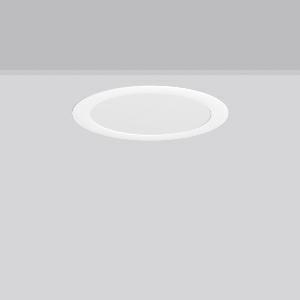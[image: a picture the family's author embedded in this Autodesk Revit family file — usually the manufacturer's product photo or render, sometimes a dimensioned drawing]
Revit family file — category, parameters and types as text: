
# Revit family: toledo_flat_round_e_672226_002_1_04_98b7
name_source: partatom
category: Lighting Fixtures
units: mm (PartAtom-declared; Revit-internal decimal feet)

## family parameters
Cut with Voids When Loaded = No
Host = Face
Light Source = No
Part Type = Normal
Room Calculation Point = No
Round Connector Dimension = Use Diameter
Shared = No

## types (1)
- TOLEDO FLAT round E (1 x LED Modul 840, 2250 lm, 4000)
    Apparent Load = 22 VA
    CIE Flux Codes = 49 80 96 100 100
    Color Rendering = 80
    Color Temperature = 4000
    Default Elevation = 1800 mm
    Description = Series: TOLEDO FLAT round
Ultra thin recessed downlight. For escape route illumination. Housing: die-cast aluminium, powder-coated. Lightguide and diffuser made of non-yellowing plastic (PMMA). Diffuser opal matt plastic. Ceiling installation with spring system. Including separate LED converter with connecting cable 250 mm. Self-contained system with automatic self-test and feedback to the RZB monitoring system MULTIDIGIT. External driver with simple plug-in locking system. 
Colour: white
Diameter: 317 mm
Height: 3 mm
Cut-out diameter: 288 mm
Recess height: 90 mm
Luminaire: recess height: 60-80 mm
Weight: 2.28 kg
Operating mode: maintained power mode
Duration time: 3 h
Lamp: LED
Socket: without socket
Colour temperature: 4000K
Colour rendering index (CRI): 80
System power: 22 W
Rated luminous flux: 2250 lm
Luminous flux, emergency: 440 lm
System power, emergency: -
Control gear: Regulated power supply
Protection class: I
Type of protection: IP 54
    Height = 0 mm  [stored 0 ft]
    Lamp = 1 x LED Modul 840
    Lamp Light Flux = 2250 lm
    Lamp count = 1
    Length = 317 mm
    Lifetime = 50000 h
    Luminous efficacy = 102 lm/W
    Manufacturer = RZB
    ModVariant = No
    Model = 672226.002.1.04
    Mounting Place = Ceiling
    Mounting Type = Recessed
    Number of Poles = 1
    OnlyDefault = Yes
    Power Factor = 1
    Product Name = TOLEDO FLAT round E
    Product group = Recessed downlights
    ProductGroupID = 402
    Protection Class = Protection class I
    Protection Degree = IP 40
    RLX_Detail_Level = 1
    RLX_Emergency_Light_Flux = 440 lm
    RLX_Emergency_Type = 3
    RLX_Emergency_Type_DB = Yes
    RlxData = <blob elided: 31681 chars, md5=0fb0789e>
    Socket = socket
    Standby Power = 0 W
    System Light Flux = 2250 lm
    System Power = 22 W
    Type Comments = Product without accessories
    Type Image = 901484.002.jpg
    URL = http://relux.com
    VarID = ---
    Voltage = 0 V
    Weight = 0.00 kg
    Width = 0 mm  [stored 0 ft]

note: [stored X ft] marks values corroborated as IEEE doubles in the binary element streams (Revit-internal decimal feet)

## geometry (parser evidence)
native form markers: Blend x4, Sweep x10
no freeform markers — native parametric forms only
